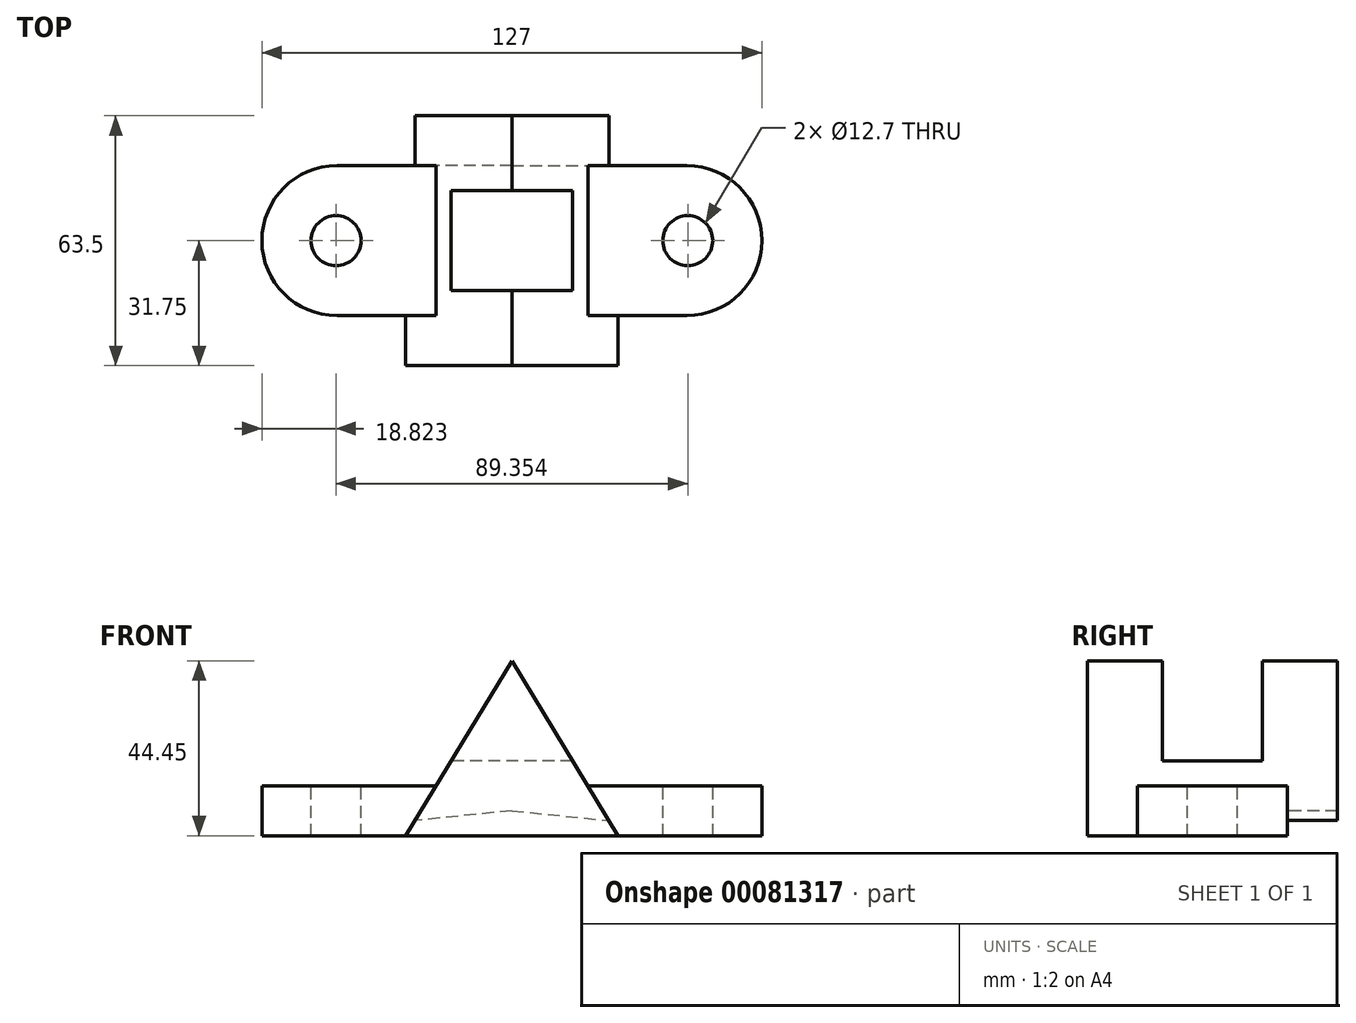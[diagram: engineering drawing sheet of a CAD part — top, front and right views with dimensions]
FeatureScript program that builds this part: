
annotation { "Feature Type Name" : "Feature", "Feature Type Description" : "" }
export const myFeature = defineFeature(function(context is Context, id is Id, definition is map)
    precondition{}
    {
        {
            var Q0;
            Q0=qCreatedBy(makeId("Top.planeOp"),FACE);
            var sketch = newSketch(context, id + "F0", { "sketchPlane" : qUnion([Q0])});
            skLineSegment(sketch, "E0.bottom", {"start": v(0, 0) * mm, "end": v(127, 0) * mm});
            skLineSegment(sketch, "E0.top", {"start": v(0, 38.1) * mm, "end": v(127, 38.1) * mm});
            skLineSegment(sketch, "E0.left", {"start": v(0, 0) * mm, "end": v(0, 38.1) * mm});
            skLineSegment(sketch, "E0.right", {"start": v(127, 0) * mm, "end": v(127, 38.1) * mm});
            skSolve(sketch);
        }
        {
            var Q0;
            Q0 = qSketchRegion(id + "F0", true);
            extrude(context, id + "F1", {"entities" : qUnion([Q0]), "depth" : 12.7 * mm});
        }
        {
            var Q0;
            Q0=makeQuery(id+"F1.opExtrude","SWEPT_FACE",FACE,{"disambiguationData":[OSD([sQuery(id+"F0.wireOp",EDGE,"E0.bottom")])]});
            var sketch = newSketch(context, id + "F2", { "sketchPlane" : qUnion([Q0])});
            skLineSegment(sketch, "E1", {"start": v(0, 0) * mm, "end": v(0, 12.7) * mm});
            skLineSegment(sketch, "E2", {"start": v(0, 12.7) * mm, "end": v(127, 12.7) * mm});
            skLineSegment(sketch, "E3", {"start": v(127, 12.7) * mm, "end": v(127, 0) * mm});
            skLineSegment(sketch, "E4", {"start": v(127, 0) * mm, "end": v(0, 0) * mm});
            skLineSegment(sketch, "E5", {"start": v(0, 0) * mm, "end": v(127, 12.7) * mm});
            skLineSegment(sketch, "E6", {"start": v(127, 0) * mm, "end": v(0, 12.7) * mm});
            skLineSegment(sketch, "E7", {"start": v(63.5, 6.35) * mm, "end": v(63.5, 0) * mm});
            skLineSegment(sketch, "E8", {"start": v(63.5, 0) * mm, "end": v(90.49, 0) * mm});
            skLineSegment(sketch, "E9", {"start": v(63.5, 0) * mm, "end": v(36.51, 0) * mm});
            skLineSegment(sketch, "E10", {"start": v(63.5, 0) * mm, "end": v(63.5, 44.45) * mm});
            skLineSegment(sketch, "E11", {"start": v(63.5, 44.45) * mm, "end": v(36.51, 0) * mm});
            skLineSegment(sketch, "E12", {"start": v(63.5, 44.45) * mm, "end": v(90.49, 0) * mm});
            skSolve(sketch);
        }
        {
            var Q0;
            {var subQ0=sQuery(id+"F2.wireOp",EDGE,"E12");var subQ1=sQuery(id+"F2.wireOp",EDGE,"E2");var subQ2=makeQuery(id+"F2.imprint","INTERSECT",VERTEX,{"derivedFrom":[subQ1,subQ0]});Q0=makeQuery(id+"F2.imprint","IMPRINT",FACE,{"disambiguationData":[TD([[makeQuery(id+"F2.imprint","IMPRINT",EDGE,{"disambiguationData":[TD([[subQ2,1.0]])],"derivedFrom":subQ1}),-1.0]])]});}
            var Q1;
            {var subQ0=sQuery(id+"F2.wireOp",EDGE,"E12");var subQ1=sQuery(id+"F2.wireOp",EDGE,"E5");var subQ2=makeQuery(id+"F2.imprint","INTERSECT",VERTEX,{"derivedFrom":[subQ1,subQ0]});Q1=makeQuery(id+"F2.imprint","IMPRINT",FACE,{"disambiguationData":[TD([[makeQuery(id+"F2.imprint","IMPRINT",EDGE,{"disambiguationData":[TD([[subQ2,-1.0]])],"derivedFrom":subQ0}),-1.0]])]});}
            var Q2;
            {var subQ5=sQuery(id+"F2.wireOp",EDGE,"E8");Q2=makeQuery(id+"F2.imprint","IMPRINT",FACE,{"disambiguationData":[TD([[makeQuery(id+"F2.imprint","IMPRINT",EDGE,{"derivedFrom":subQ5}),1.0]])]});}
            var Q3;
            {var subQ5=sQuery(id+"F2.wireOp",EDGE,"E9");Q3=makeQuery(id+"F2.imprint","IMPRINT",FACE,{"disambiguationData":[TD([[makeQuery(id+"F2.imprint","IMPRINT",EDGE,{"derivedFrom":subQ5}),1.0]])]});}
            var Q4;
            {var subQ0=sQuery(id+"F2.wireOp",EDGE,"E11");var subQ1=sQuery(id+"F2.wireOp",EDGE,"E5");var subQ2=makeQuery(id+"F2.imprint","INTERSECT",VERTEX,{"derivedFrom":[subQ1,subQ0]});Q4=makeQuery(id+"F2.imprint","IMPRINT",FACE,{"disambiguationData":[TD([[makeQuery(id+"F2.imprint","IMPRINT",EDGE,{"disambiguationData":[TD([[subQ2,1.0]])],"derivedFrom":subQ0}),1.0]])]});}
            var Q5;
            {var subQ0=sQuery(id+"F2.wireOp",EDGE,"E11");var subQ1=sQuery(id+"F2.wireOp",EDGE,"E2");var subQ2=makeQuery(id+"F2.imprint","INTERSECT",VERTEX,{"derivedFrom":[subQ1,subQ0]});Q5=makeQuery(id+"F2.imprint","IMPRINT",FACE,{"disambiguationData":[TD([[makeQuery(id+"F2.imprint","IMPRINT",EDGE,{"disambiguationData":[TD([[subQ2,-1.0]])],"derivedFrom":subQ1}),-1.0]])]});}
            var Q6;
            {var subQ0=sQuery(id+"F2.wireOp",EDGE,"E11");var subQ1=sQuery(id+"F2.wireOp",EDGE,"E2");var subQ2=makeQuery(id+"F2.imprint","INTERSECT",VERTEX,{"derivedFrom":[subQ1,subQ0]});Q6=makeQuery(id+"F2.imprint","IMPRINT",FACE,{"disambiguationData":[TD([[makeQuery(id+"F2.imprint","IMPRINT",EDGE,{"disambiguationData":[TD([[subQ2,-1.0]])],"derivedFrom":subQ1}),1.0]])]});}
            var Q7;
            {var subQ0=sQuery(id+"F2.wireOp",EDGE,"E12");var subQ1=sQuery(id+"F2.wireOp",EDGE,"E2");var subQ2=makeQuery(id+"F2.imprint","INTERSECT",VERTEX,{"derivedFrom":[subQ1,subQ0]});Q7=makeQuery(id+"F2.imprint","IMPRINT",FACE,{"disambiguationData":[TD([[makeQuery(id+"F2.imprint","IMPRINT",EDGE,{"disambiguationData":[TD([[subQ2,1.0]])],"derivedFrom":subQ1}),1.0]])]});}
            extrude(context, id + "F3", {"entities" : qUnion([Q0, Q1, Q2, Q3, Q4, Q5, Q6, Q7]), "operationType" : NewBodyOperationType.ADD, "oppositeDirection" : true, "depth" : 50.8 * mm});
        }
        {
            var Q0;
            Q0=makeQuery(id+"F3.boolean.opBoolean","MERGE",FACE,{"derivedFrom":[makeQuery(id+"F1.opExtrude","SWEPT_FACE",FACE,{"disambiguationData":[OSD([sQuery(id+"F0.wireOp",EDGE,"E0.bottom")])]}),makeQuery(id+"F3.opExtrude","CAP_FACE",FACE,{"disambiguationData":[OSD([sQuery(id+"F2.wireOp",EDGE,"E8"),sQuery(id+"F2.wireOp",EDGE,"E9"),sQuery(id+"F2.wireOp",EDGE,"E11"),sQuery(id+"F2.wireOp",EDGE,"E12")])],"isStart":true})]});
            var sketch = newSketch(context, id + "F4", { "sketchPlane" : qUnion([Q0])});
            skLineSegment(sketch, "E13", {"start": v(63.5, 44.45) * mm, "end": v(36.51, 0) * mm});
            skLineSegment(sketch, "E14", {"start": v(63.5, 44.45) * mm, "end": v(90.49, 0) * mm});
            skLineSegment(sketch, "E15", {"start": v(90.49, 0) * mm, "end": v(36.51, 0) * mm});
            skSolve(sketch);
        }
        {
            var Q0;
            Q0 = qSketchRegion(id + "F4", true);
            extrude(context, id + "F5", {"entities" : qUnion([Q0]), "operationType" : NewBodyOperationType.ADD, "depth" : 12.7 * mm});
        }
        {
            var Q0;
            Q0=makeQuery(id+"F1.opExtrude","SWEPT_EDGE",EDGE,{"disambiguationData":[OSD([sQuery(id+"F0.wireOp",EDGE,"E0.bottom"),sQuery(id+"F0.wireOp",EDGE,"E0.left")])]});
            var Q1;
            Q1=makeQuery(id+"F1.opExtrude","SWEPT_EDGE",EDGE,{"disambiguationData":[OSD([sQuery(id+"F0.wireOp",EDGE,"E0.top"),sQuery(id+"F0.wireOp",EDGE,"E0.left")])]});
            var Q2;
            Q2=makeQuery(id+"F1.opExtrude","SWEPT_EDGE",EDGE,{"disambiguationData":[OSD([sQuery(id+"F0.wireOp",EDGE,"E0.top"),sQuery(id+"F0.wireOp",EDGE,"E0.right")])]});
            var Q3;
            Q3=makeQuery(id+"F1.opExtrude","SWEPT_EDGE",EDGE,{"disambiguationData":[OSD([sQuery(id+"F0.wireOp",EDGE,"E0.bottom"),sQuery(id+"F0.wireOp",EDGE,"E0.right")])]});
            fillet(context, id + "F6", {"entities" : qUnion([Q0, Q1, Q2, Q3]), "radius" : 19.05 * mm, "tangentPropagation" : true, "allowEdgeOverflow" : false});
        }
        {
            var Q0;
            {var subQ0=sQuery(id+"F0.wireOp",EDGE,"E0.left");var subQ2=sQuery(id+"F0.wireOp",EDGE,"E0.top");var subQ3=sQuery(id+"F0.wireOp",EDGE,"E0.bottom");Q0=makeQuery(id+"F3.boolean.opBoolean","SPLIT",FACE,{"disambiguationData":[TD([makeQuery(id+"F1.opExtrude","SWEPT_FACE",FACE,{"disambiguationData":[OSD([subQ0])]})])],"derivedFrom":makeQuery(id+"F1.opExtrude","CAP_FACE",FACE,{"disambiguationData":[OSD([subQ3,subQ2,subQ0,sQuery(id+"F0.wireOp",EDGE,"E0.right")])],"isStart":false})});}
            var sketch = newSketch(context, id + "F7", { "sketchPlane" : qUnion([Q0])});
            skLineSegment(sketch, "E16", {"start": v(44.22, 19.05) * mm, "end": v(18.82, 19.05) * mm});
            skSolve(sketch);
        }
        {
            var Q0;
            Q0=sQuery(id+"F7.wireOp",VERTEX,"E16.end");
            var Q1;
            Q1=makeQuery(id+"F1.opExtrude","SWEPT_BODY",BODY,{"disambiguationData":[OSD([sQuery(id+"F0.wireOp",EDGE,"E0.bottom"),sQuery(id+"F0.wireOp",EDGE,"E0.top"),sQuery(id+"F0.wireOp",EDGE,"E0.left"),sQuery(id+"F0.wireOp",EDGE,"E0.right")])]});
            hole(context, id + "F8", {"style" : HoleStyle.SIMPLE, "endStyle" : HoleEndStyle.THROUGH, "holeDiameter" : 12.7 * mm, "locations" : qUnion([Q0]), "scope" : qUnion([Q1]), "isTappedThrough" : true});
        }
        {
            var Q0;
            Q0=qCreatedBy(makeId("Right.planeOp"),FACE);
            cPlane(context, id + "F9", {"entities" : qUnion([Q0]), "cplaneType" : CPlaneType.OFFSET, "offset" : 63.5 * mm, "width" : 152.4 * mm, "height" : 152.4 * mm});
        }
        {
            var Q0;
            {var subQ0=sQuery(id+"F0.wireOp",EDGE,"E0.right");var subQ1=sQuery(id+"F0.wireOp",EDGE,"E0.top");var subQ3=sQuery(id+"F0.wireOp",EDGE,"E0.bottom");Q0=makeQuery(id+"F3.boolean.opBoolean","SPLIT",FACE,{"disambiguationData":[TD([makeQuery(id+"F1.opExtrude","SWEPT_FACE",FACE,{"disambiguationData":[OSD([subQ0])]})])],"derivedFrom":makeQuery(id+"F1.opExtrude","CAP_FACE",FACE,{"disambiguationData":[OSD([subQ3,subQ1,sQuery(id+"F0.wireOp",EDGE,"E0.left"),subQ0])],"isStart":false})});}
            var sketch = newSketch(context, id + "F10", { "sketchPlane" : qUnion([Q0])});
            skLineSegment(sketch, "E17", {"start": v(82.78, 19.05) * mm, "end": v(108.18, 19.05) * mm});
            skSolve(sketch);
        }
        {
            var Q0;
            Q0=sQuery(id+"F10.wireOp",VERTEX,"E17.end");
            var Q1;
            Q1=makeQuery(id+"F1.opExtrude","SWEPT_BODY",BODY,{"disambiguationData":[OSD([sQuery(id+"F0.wireOp",EDGE,"E0.bottom"),sQuery(id+"F0.wireOp",EDGE,"E0.top"),sQuery(id+"F0.wireOp",EDGE,"E0.left"),sQuery(id+"F0.wireOp",EDGE,"E0.right")])]});
            hole(context, id + "F11", {"style" : HoleStyle.SIMPLE, "endStyle" : HoleEndStyle.THROUGH, "holeDiameter" : 12.7 * mm, "locations" : qUnion([Q0]), "scope" : qUnion([Q1]), "isTappedThrough" : true});
        }
        {
            var Q0;
            Q0=qCreatedBy(id+"F9.planeOp",FACE);
            var sketch = newSketch(context, id + "F12", { "sketchPlane" : qUnion([Q0])});
            skLineSegment(sketch, "E18", {"start": v(0, 0) * mm, "end": v(0, 44.45) * mm});
            skLineSegment(sketch, "E19", {"start": v(0, 44.45) * mm, "end": v(-12.7, 44.45) * mm});
            skLineSegment(sketch, "E20", {"start": v(-12.7, 44.45) * mm, "end": v(6.35, 44.45) * mm});
            skLineSegment(sketch, "E21", {"start": v(6.35, 44.45) * mm, "end": v(6.35, 19.05) * mm});
            skLineSegment(sketch, "E22", {"start": v(6.35, 19.05) * mm, "end": v(31.75, 19.05) * mm});
            skLineSegment(sketch, "E23", {"start": v(31.75, 19.05) * mm, "end": v(31.75, 44.45) * mm});
            skLineSegment(sketch, "E24", {"start": v(31.75, 44.45) * mm, "end": v(6.35, 44.45) * mm});
            skSolve(sketch);
        }
        {
            var Q0;
            Q0 = qSketchRegion(id + "F12", true);
            extrude(context, id + "F13", {"entities" : qUnion([Q0]), "operationType" : NewBodyOperationType.REMOVE, "endBound" : BoundingType.SYMMETRIC, "depth" : 50.8 * mm});
        }
    });
